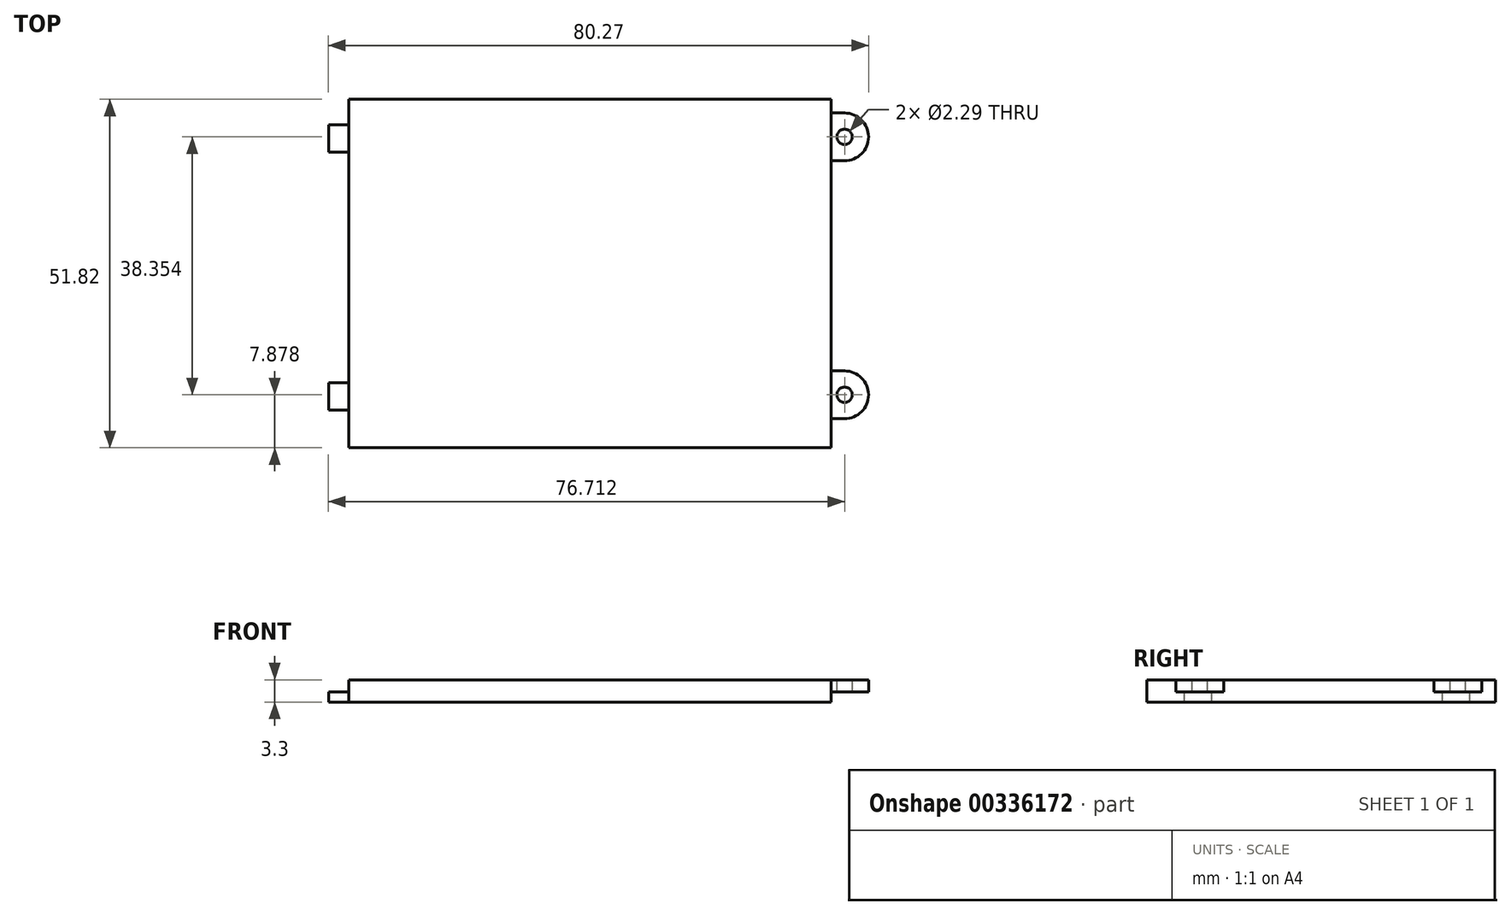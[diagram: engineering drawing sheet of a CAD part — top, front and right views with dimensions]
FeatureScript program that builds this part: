
annotation { "Feature Type Name" : "Feature", "Feature Type Description" : "" }
export const myFeature = defineFeature(function(context is Context, id is Id, definition is map)
    precondition{}
    {
        {
            var Q0;
            Q0=qCreatedBy(makeId("Top.planeOp"),FACE);
            var sketch = newSketch(context, id + "F0", { "sketchPlane" : qUnion([Q0])});
            skLineSegment(sketch, "E0.bottom", {"start": v(0, 0) * mm, "end": v(-71.63, 0) * mm});
            skLineSegment(sketch, "E0.top", {"start": v(0, -51.82) * mm, "end": v(-71.63, -51.82) * mm});
            skLineSegment(sketch, "E0.left", {"start": v(0, 0) * mm, "end": v(0, -51.82) * mm});
            skLineSegment(sketch, "E0.right", {"start": v(-71.63, 0) * mm, "end": v(-71.63, -51.82) * mm});
            skSolve(sketch);
        }
        {
            var Q0;
            Q0 = qSketchRegion(id + "F0", true);
            extrude(context, id + "F1", {"entities" : qUnion([Q0]), "depth" : 3.3 * mm});
        }
        {
            var Q0;
            Q0=makeQuery(id+"F1.opExtrude","CAP_FACE",FACE,{"disambiguationData":[OSD([sQuery(id+"F0.wireOp",EDGE,"E0.bottom"),sQuery(id+"F0.wireOp",EDGE,"E0.top"),sQuery(id+"F0.wireOp",EDGE,"E0.left"),sQuery(id+"F0.wireOp",EDGE,"E0.right")])],"isStart":false});
            var sketch = newSketch(context, id + "F2", { "sketchPlane" : qUnion([Q0])});
            skLineSegment(sketch, "E1", {"start": v(0, -2.03) * mm, "end": v(2.03, -2.03) * mm});
            skLineSegment(sketch, "E2", {"start": v(0, -9.14) * mm, "end": v(2.03, -9.14) * mm});
            skArc(sketch, "E3", {"start": v(2.03, -9.14) * mm, "mid": v(5.59, -5.59) * mm, "end": v(2.03, -2.03) * mm});
            skLineSegment(sketch, "E4", {"start": v(0, -9.14) * mm, "end": v(0, -2.03) * mm});
            skLineSegment(sketch, "E5", {"start": v(2.03, -40.39) * mm, "end": v(0, -40.39) * mm});
            skLineSegment(sketch, "E6", {"start": v(0, -40.39) * mm, "end": v(0, -47.5) * mm});
            skLineSegment(sketch, "E7", {"start": v(0, -47.5) * mm, "end": v(2.03, -47.5) * mm});
            skArc(sketch, "E8", {"start": v(2.03, -47.5) * mm, "mid": v(5.59, -43.94) * mm, "end": v(2.03, -40.39) * mm});
            skCircle(sketch, "E9", {"center": v(2.03, -5.59) * mm, "radius": 1.14 * mm});
            skCircle(sketch, "E10", {"center": v(2.03, -43.94) * mm, "radius": 1.14 * mm});
            skSolve(sketch);
        }
        {
            var Q0;
            Q0 = qSketchRegion(id + "F2", true);
            extrude(context, id + "F3", {"entities" : qUnion([Q0]), "oppositeDirection" : true, "depth" : 1.78 * mm});
        }
        {
            var Q0;
            Q0=makeQuery(id+"F1.opExtrude","CAP_FACE",FACE,{"disambiguationData":[OSD([sQuery(id+"F0.wireOp",EDGE,"E0.bottom"),sQuery(id+"F0.wireOp",EDGE,"E0.top"),sQuery(id+"F0.wireOp",EDGE,"E0.left"),sQuery(id+"F0.wireOp",EDGE,"E0.right")])],"isStart":false});
            var sketch = newSketch(context, id + "F4", { "sketchPlane" : qUnion([Q0])});
            skLineSegment(sketch, "E11.bottom", {"start": v(-71.63, -3.8) * mm, "end": v(-74.68, -3.81) * mm});
            skLineSegment(sketch, "E11.top", {"start": v(-71.63, -7.87) * mm, "end": v(-74.68, -7.87) * mm});
            skLineSegment(sketch, "E11.left", {"start": v(-71.63, -3.8) * mm, "end": v(-71.63, -7.87) * mm});
            skLineSegment(sketch, "E11.right", {"start": v(-74.68, -3.81) * mm, "end": v(-74.68, -7.87) * mm});
            skLineSegment(sketch, "E12.bottom", {"start": v(-71.63, -42.16) * mm, "end": v(-74.68, -42.16) * mm});
            skLineSegment(sketch, "E12.top", {"start": v(-71.63, -46.23) * mm, "end": v(-74.68, -46.23) * mm});
            skLineSegment(sketch, "E12.left", {"start": v(-71.63, -42.16) * mm, "end": v(-71.63, -46.23) * mm});
            skLineSegment(sketch, "E12.right", {"start": v(-74.68, -42.16) * mm, "end": v(-74.68, -46.23) * mm});
            skSolve(sketch);
        }
        {
            var Q0;
            Q0 = qSketchRegion(id + "F4", true);
            extrude(context, id + "F5", {"entities" : qUnion([Q0]), "oppositeDirection" : true, "depth" : 3.3 * mm});
        }
        {
            var Q0;
            Q0=makeQuery(id+"F5.opExtrude","SWEPT_FACE",FACE,{"disambiguationData":[OSD([sQuery(id+"F4.wireOp",EDGE,"E12.top")])]});
            var sketch = newSketch(context, id + "F6", { "sketchPlane" : qUnion([Q0])});
            skLineSegment(sketch, "E13.bottom", {"start": v(-71.63, 3.3) * mm, "end": v(-74.68, 3.3) * mm});
            skLineSegment(sketch, "E13.top", {"start": v(-71.63, 1.52) * mm, "end": v(-74.68, 1.52) * mm});
            skLineSegment(sketch, "E13.left", {"start": v(-71.63, 3.3) * mm, "end": v(-71.63, 1.52) * mm});
            skLineSegment(sketch, "E13.right", {"start": v(-74.68, 3.3) * mm, "end": v(-74.68, 1.52) * mm});
            skSolve(sketch);
        }
        {
            var Q0;
            Q0 = qSketchRegion(id + "F6", true);
            extrude(context, id + "F7", {"entities" : qUnion([Q0]), "operationType" : NewBodyOperationType.REMOVE, "oppositeDirection" : true, "depth" : 101.6 * mm});
        }
    });
